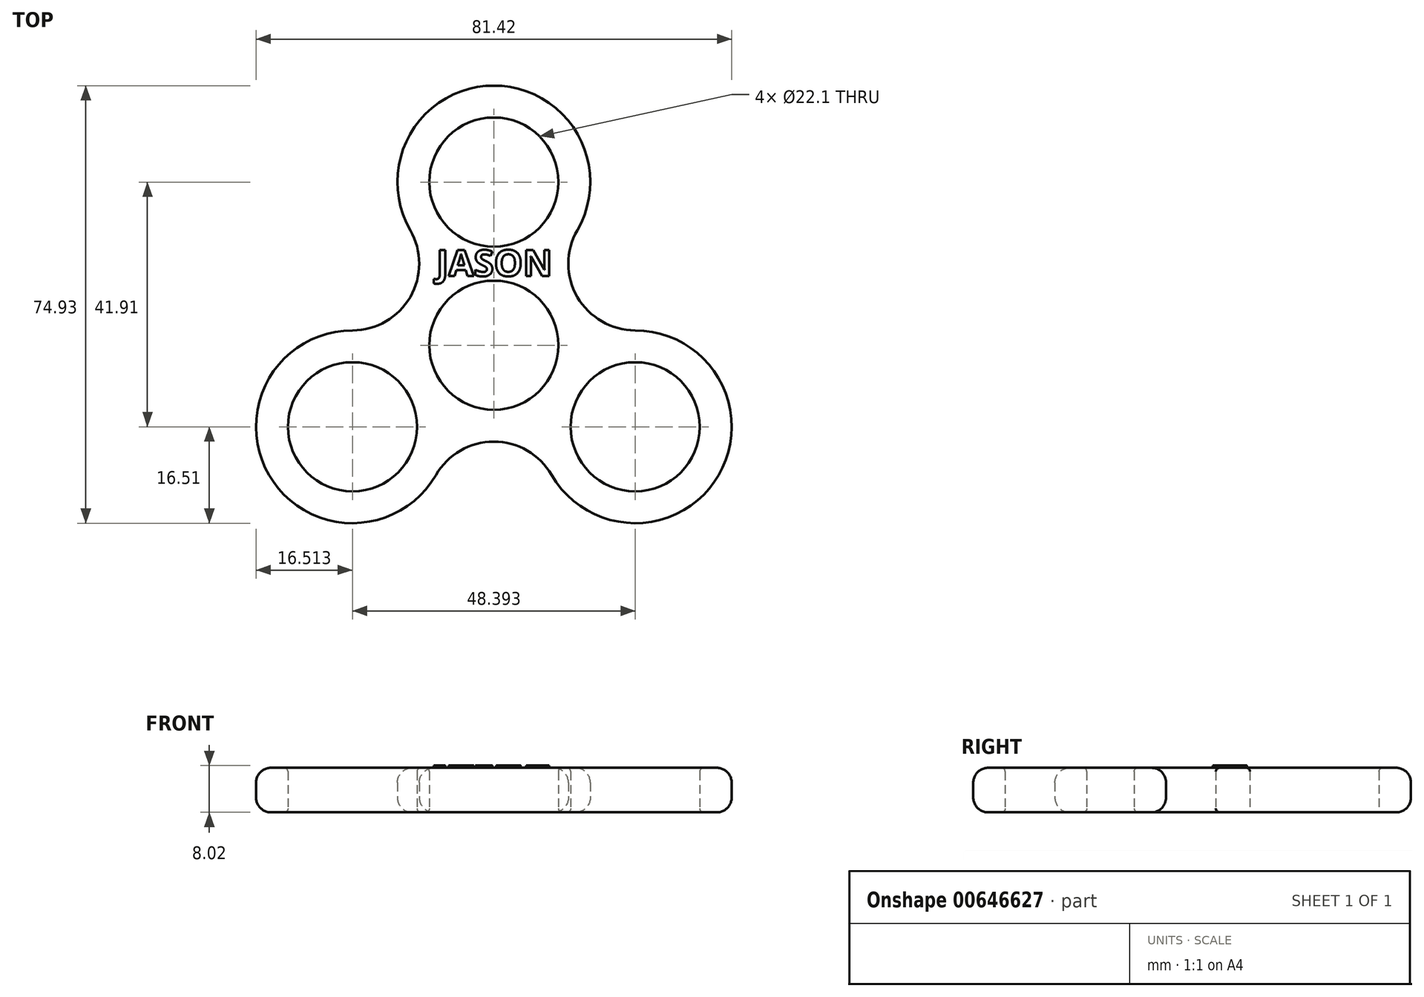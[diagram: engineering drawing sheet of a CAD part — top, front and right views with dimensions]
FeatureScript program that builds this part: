
annotation { "Feature Type Name" : "Feature", "Feature Type Description" : "" }
export const myFeature = defineFeature(function(context is Context, id is Id, definition is map)
    precondition{}
    {
        {
            var Q0;
            Q0=qCreatedBy(makeId("Top.planeOp"),FACE);
            var sketch = newSketch(context, id + "F0", { "sketchPlane" : qUnion([Q0])});
            skCircle(sketch, "E0", {"center": v(0, 0) * mm, "radius": 11.05 * mm});
            skCircle(sketch, "E1", {"center": v(0, 27.94) * mm, "radius": 11.05 * mm});
            skCircle(sketch, "E2.1.0", {"center": v(-24.2, -13.97) * mm, "radius": 11.05 * mm});
            skCircle(sketch, "E2.2.0", {"center": v(24.2, -13.97) * mm, "radius": 11.05 * mm});
            skArc(sketch, "E3", {"start": v(14.3, 19.69) * mm, "mid": v(0, 44.45) * mm, "end": v(-14.3, 19.69) * mm});
            skArc(sketch, "E4.1.0", {"start": v(-24.2, 2.54) * mm, "mid": v(-38.5, -22.22) * mm, "end": v(-9.9, -22.23) * mm});
            skArc(sketch, "E4.2.0", {"start": v(9.9, -22.23) * mm, "mid": v(38.5, -22.23) * mm, "end": v(24.2, 2.54) * mm});
            skArc(sketch, "E5", {"start": v(-24.2, 2.54) * mm, "mid": v(-14.3, 8.26) * mm, "end": v(-14.3, 19.69) * mm});
            skArc(sketch, "E6.1.0", {"start": v(9.9, -22.23) * mm, "mid": v(0, -16.51) * mm, "end": v(-9.9, -22.23) * mm});
            skArc(sketch, "E6.2.0", {"start": v(14.3, 19.68) * mm, "mid": v(14.3, 8.25) * mm, "end": v(24.2, 2.54) * mm});
            skSolve(sketch);
        }
        {
            var Q0;
            Q0=qSketchRegion(id+"F0",true);
            extrude(context, id + "F1", {"entities" : qUnion([Q0]), "depth" : 7.62 * mm, "offsetDistance" : 25.4 * mm});
        }
        {
            var Q0;
            Q0=makeQuery(id+"F1.opExtrude","CAP_EDGE",EDGE,{"disambiguationData":[OSD([sQuery(id+"F0.wireOp",EDGE,"E0")])],"isStart":false});
            var Q1;
            Q1=makeQuery(id+"F1.opExtrude","CAP_EDGE",EDGE,{"disambiguationData":[OSD([sQuery(id+"F0.wireOp",EDGE,"E0")])],"isStart":true});
            var Q2;
            Q2=makeQuery(id+"F1.opExtrude","CAP_EDGE",EDGE,{"disambiguationData":[OSD([sQuery(id+"F0.wireOp",EDGE,"E2.2.0")])],"isStart":true});
            var Q3;
            Q3=makeQuery(id+"F1.opExtrude","CAP_EDGE",EDGE,{"disambiguationData":[OSD([sQuery(id+"F0.wireOp",EDGE,"E2.1.0")])],"isStart":true});
            var Q4;
            Q4=makeQuery(id+"F1.opExtrude","CAP_EDGE",EDGE,{"disambiguationData":[OSD([sQuery(id+"F0.wireOp",EDGE,"E2.1.0")])],"isStart":false});
            var Q5;
            Q5=makeQuery(id+"F1.opExtrude","CAP_EDGE",EDGE,{"disambiguationData":[OSD([sQuery(id+"F0.wireOp",EDGE,"E2.2.0")])],"isStart":false});
            var Q6;
            Q6=makeQuery(id+"F1.opExtrude","CAP_EDGE",EDGE,{"disambiguationData":[OSD([sQuery(id+"F0.wireOp",EDGE,"E1")])],"isStart":false});
            fillet(context, id + "F2", {"entities" : qUnion([Q0, Q1, Q2, Q3, Q4, Q5, Q6]), "radius" : 0.64 * mm, "tangentPropagation" : true, "allowEdgeOverflow" : false});
        }
        {
            var Q0;
            Q0=makeQuery(id+"F1.opExtrude","CAP_EDGE",EDGE,{"disambiguationData":[OSD([sQuery(id+"F0.wireOp",EDGE,"E4.1.0")])],"isStart":false});
            var Q1;
            Q1=makeQuery(id+"F1.opExtrude","CAP_EDGE",EDGE,{"disambiguationData":[OSD([sQuery(id+"F0.wireOp",EDGE,"E4.1.0")])],"isStart":true});
            fillet(context, id + "F3", {"entities" : qUnion([Q0, Q1]), "radius" : 2.54 * mm, "tangentPropagation" : true, "allowEdgeOverflow" : false});
        }
        {
            var Q0;
            Q0=makeQuery(id+"F1.opExtrude","CAP_FACE",FACE,{"disambiguationData":[OSD([sQuery(id+"F0.wireOp",EDGE,"E0"),sQuery(id+"F0.wireOp",EDGE,"E1"),sQuery(id+"F0.wireOp",EDGE,"E2.1.0"),sQuery(id+"F0.wireOp",EDGE,"E2.2.0"),sQuery(id+"F0.wireOp",EDGE,"E3"),sQuery(id+"F0.wireOp",EDGE,"E4.1.0"),sQuery(id+"F0.wireOp",EDGE,"E4.2.0"),sQuery(id+"F0.wireOp",EDGE,"E5"),sQuery(id+"F0.wireOp",EDGE,"E6.1.0"),sQuery(id+"F0.wireOp",EDGE,"E6.2.0")])],"isStart":false});
            var sketch = newSketch(context, id + "F4", { "sketchPlane" : qUnion([Q0])});
            skText(sketch, "E7", { "text": "JASON", "fontName": "OpenSans-Bold.ttf"});
            const initialGuessF4  = {"E7": [-0.00983, 0.01182, 1, 0, 0.0045]};
            skSetInitialGuess(sketch, initialGuessF4);
            skSolve(sketch);
        }
        {
            var Q0;
            Q0 = qSketchRegion(id + "F4", true);
            extrude(context, id + "F5", {"entities" : qUnion([Q0]), "operationType" : NewBodyOperationType.ADD, "depth" : 0.4 * mm, "offsetDistance" : 25.4 * mm});
        }
    });
